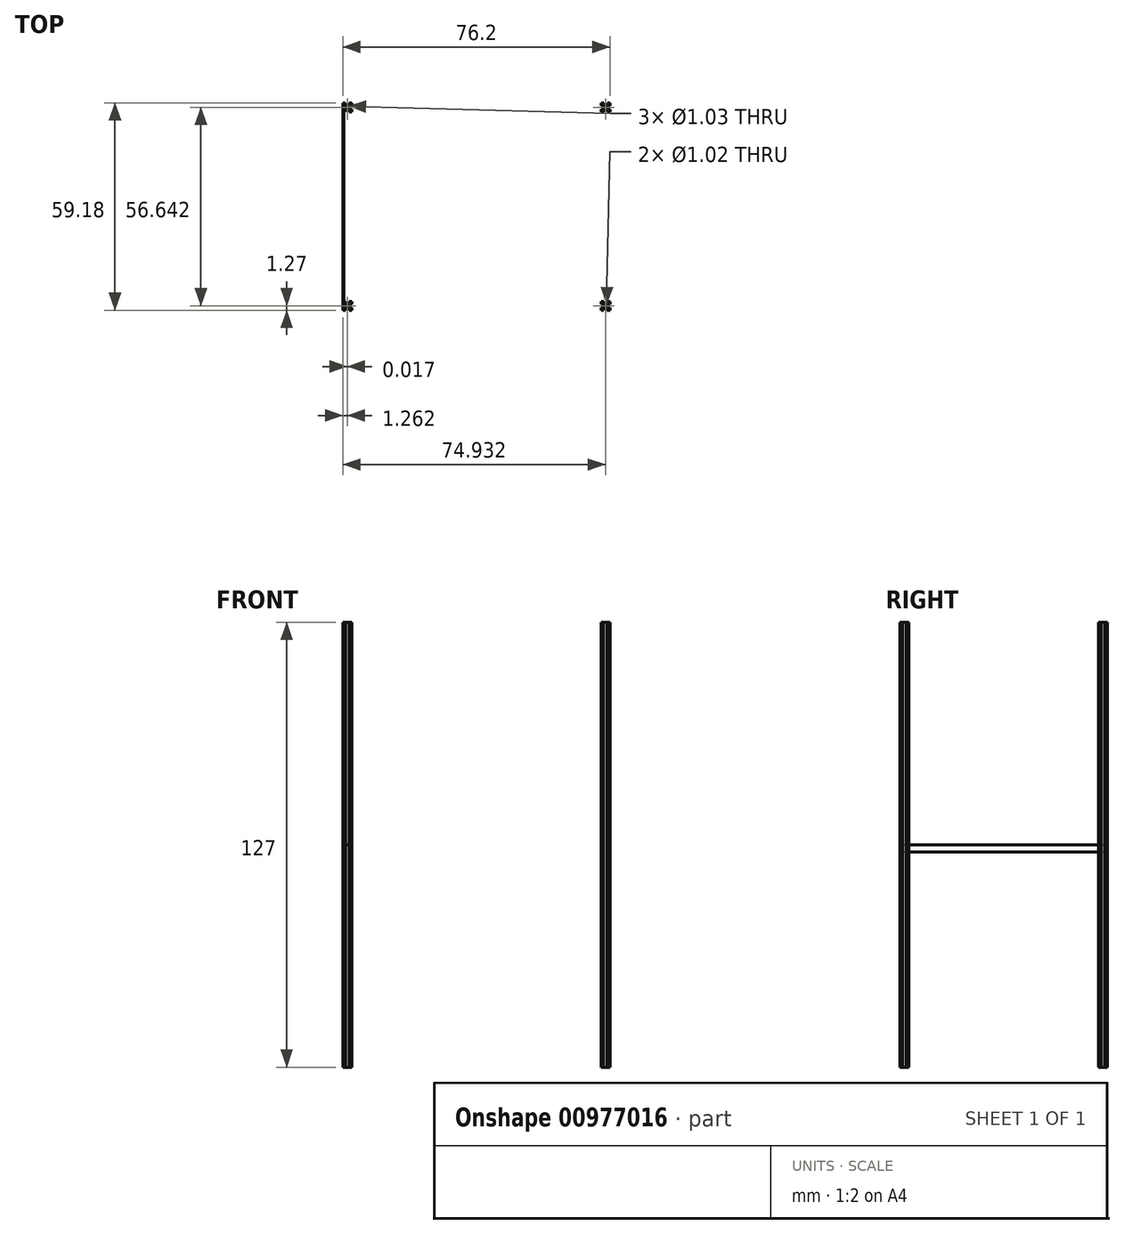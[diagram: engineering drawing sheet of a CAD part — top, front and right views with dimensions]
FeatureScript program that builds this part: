
annotation { "Feature Type Name" : "Feature", "Feature Type Description" : "" }
export const myFeature = defineFeature(function(context is Context, id is Id, definition is map)
    precondition{}
    {
        {
            var Q0;
            Q0=qCreatedBy(makeId("Top.planeOp"),FACE);
            var sketch = newSketch(context, id + "F0", { "sketchPlane" : qUnion([Q0])});
            skLineSegment(sketch, "E0.bottom", {"start": v(0, 0) * mm, "end": v(76.2, 0) * mm});
            skLineSegment(sketch, "E0.top", {"start": v(0, 59.18) * mm, "end": v(76.2, 59.18) * mm});
            skLineSegment(sketch, "E0.left", {"start": v(0, 0) * mm, "end": v(0, 59.18) * mm});
            skLineSegment(sketch, "E0.right", {"start": v(76.2, 0) * mm, "end": v(76.2, 59.18) * mm});
            skLineSegment(sketch, "E1.bottom", {"start": v(0, 59.18) * mm, "end": v(2.54, 59.18) * mm});
            skLineSegment(sketch, "E1.top", {"start": v(0, 56.64) * mm, "end": v(2.54, 56.64) * mm});
            skLineSegment(sketch, "E1.left", {"start": v(0, 59.18) * mm, "end": v(0, 56.64) * mm});
            skLineSegment(sketch, "E1.right", {"start": v(2.54, 59.18) * mm, "end": v(2.54, 56.64) * mm});
            skLineSegment(sketch, "E2.bottom", {"start": v(76.2, 59.18) * mm, "end": v(73.66, 59.18) * mm});
            skLineSegment(sketch, "E2.top", {"start": v(76.2, 56.64) * mm, "end": v(73.66, 56.64) * mm});
            skLineSegment(sketch, "E2.left", {"start": v(76.2, 59.18) * mm, "end": v(76.2, 56.64) * mm});
            skLineSegment(sketch, "E2.right", {"start": v(73.66, 59.18) * mm, "end": v(73.66, 56.64) * mm});
            skLineSegment(sketch, "E3.bottom", {"start": v(0, 0) * mm, "end": v(2.54, 0) * mm});
            skLineSegment(sketch, "E3.top", {"start": v(0, 2.54) * mm, "end": v(2.54, 2.54) * mm});
            skLineSegment(sketch, "E3.left", {"start": v(0, 0) * mm, "end": v(0, 2.54) * mm});
            skLineSegment(sketch, "E3.right", {"start": v(2.54, 0) * mm, "end": v(2.54, 2.54) * mm});
            skLineSegment(sketch, "E4.bottom", {"start": v(76.2, 0) * mm, "end": v(73.66, 0) * mm});
            skLineSegment(sketch, "E4.top", {"start": v(76.2, 2.54) * mm, "end": v(73.66, 2.54) * mm});
            skLineSegment(sketch, "E4.left", {"start": v(76.2, 0) * mm, "end": v(76.2, 2.54) * mm});
            skLineSegment(sketch, "E4.right", {"start": v(73.66, 0) * mm, "end": v(73.66, 2.54) * mm});
            skLineSegment(sketch, "E5", {"start": v(0, 57.91) * mm, "end": v(1.26, 57.91) * mm});
            skCircle(sketch, "E6", {"center": v(1.26, 57.91) * mm, "radius": 0.52 * mm});
            skLineSegment(sketch, "E7.bottom", {"start": v(0.74, 59.18) * mm, "end": v(1.79, 59.18) * mm});
            skLineSegment(sketch, "E7.top", {"start": v(0.74, 58.68) * mm, "end": v(1.79, 58.68) * mm});
            skLineSegment(sketch, "E7.left", {"start": v(0.74, 59.18) * mm, "end": v(0.74, 58.68) * mm});
            skLineSegment(sketch, "E7.right", {"start": v(1.79, 59.18) * mm, "end": v(1.79, 58.68) * mm});
            skLineSegment(sketch, "E8.bottom", {"start": v(2.54, 58.42) * mm, "end": v(2.04, 58.42) * mm});
            skLineSegment(sketch, "E8.top", {"start": v(2.54, 57.37) * mm, "end": v(2.04, 57.37) * mm});
            skLineSegment(sketch, "E8.left", {"start": v(2.54, 58.42) * mm, "end": v(2.54, 57.37) * mm});
            skLineSegment(sketch, "E8.right", {"start": v(2.04, 58.42) * mm, "end": v(2.04, 57.37) * mm});
            skLineSegment(sketch, "E9.bottom", {"start": v(0.74, 56.64) * mm, "end": v(1.79, 56.64) * mm});
            skLineSegment(sketch, "E9.top", {"start": v(0.74, 57.14) * mm, "end": v(1.79, 57.14) * mm});
            skLineSegment(sketch, "E9.left", {"start": v(0.74, 56.64) * mm, "end": v(0.74, 57.14) * mm});
            skLineSegment(sketch, "E9.right", {"start": v(1.79, 56.64) * mm, "end": v(1.79, 57.14) * mm});
            skLineSegment(sketch, "E10.bottom", {"start": v(0, 57.37) * mm, "end": v(0.5, 57.37) * mm});
            skLineSegment(sketch, "E10.top", {"start": v(0, 58.4) * mm, "end": v(0.5, 58.4) * mm});
            skLineSegment(sketch, "E10.left", {"start": v(0, 57.37) * mm, "end": v(0, 58.4) * mm});
            skLineSegment(sketch, "E10.right", {"start": v(0.5, 57.37) * mm, "end": v(0.5, 58.4) * mm});
            skLineSegment(sketch, "E11", {"start": v(73.66, 57.91) * mm, "end": v(74.93, 57.91) * mm});
            skCircle(sketch, "E12", {"center": v(74.93, 57.91) * mm, "radius": 0.5 * mm});
            skLineSegment(sketch, "E13.bottom", {"start": v(76.2, 58.39) * mm, "end": v(75.7, 58.39) * mm});
            skLineSegment(sketch, "E13.top", {"start": v(76.2, 57.38) * mm, "end": v(75.7, 57.38) * mm});
            skLineSegment(sketch, "E13.left", {"start": v(76.2, 58.39) * mm, "end": v(76.2, 57.38) * mm});
            skLineSegment(sketch, "E13.right", {"start": v(75.7, 58.39) * mm, "end": v(75.7, 57.38) * mm});
            skLineSegment(sketch, "E14.bottom", {"start": v(73.66, 57.38) * mm, "end": v(74.16, 57.38) * mm});
            skLineSegment(sketch, "E14.top", {"start": v(73.66, 58.4) * mm, "end": v(74.16, 58.4) * mm});
            skLineSegment(sketch, "E14.left", {"start": v(73.66, 57.38) * mm, "end": v(73.66, 58.4) * mm});
            skLineSegment(sketch, "E14.right", {"start": v(74.16, 57.38) * mm, "end": v(74.16, 58.4) * mm});
            skLineSegment(sketch, "E15", {"start": v(73.66, 1.27) * mm, "end": v(74.93, 1.27) * mm});
            skCircle(sketch, "E16", {"center": v(74.93, 1.27) * mm, "radius": 0.51 * mm});
            skLineSegment(sketch, "E17.bottom", {"start": v(76.2, 1.75) * mm, "end": v(75.7, 1.75) * mm});
            skLineSegment(sketch, "E17.top", {"start": v(76.2, 0.73) * mm, "end": v(75.7, 0.73) * mm});
            skLineSegment(sketch, "E17.left", {"start": v(76.2, 1.75) * mm, "end": v(76.2, 0.73) * mm});
            skLineSegment(sketch, "E17.right", {"start": v(75.7, 1.75) * mm, "end": v(75.7, 0.73) * mm});
            skLineSegment(sketch, "E18.bottom", {"start": v(73.66, 1.75) * mm, "end": v(74.16, 1.75) * mm});
            skLineSegment(sketch, "E18.top", {"start": v(73.66, 0.73) * mm, "end": v(74.16, 0.73) * mm});
            skLineSegment(sketch, "E18.left", {"start": v(73.66, 1.75) * mm, "end": v(73.66, 0.73) * mm});
            skLineSegment(sketch, "E18.right", {"start": v(74.16, 1.75) * mm, "end": v(74.16, 0.73) * mm});
            skLineSegment(sketch, "E19", {"start": v(0, 1.27) * mm, "end": v(1.28, 1.27) * mm});
            skCircle(sketch, "E20", {"center": v(1.28, 1.27) * mm, "radius": 0.51 * mm});
            skLineSegment(sketch, "E21.bottom", {"start": v(0.77, 2.54) * mm, "end": v(1.79, 2.54) * mm});
            skLineSegment(sketch, "E21.top", {"start": v(0.77, 2.04) * mm, "end": v(1.79, 2.04) * mm});
            skLineSegment(sketch, "E21.left", {"start": v(0.77, 2.54) * mm, "end": v(0.77, 2.04) * mm});
            skLineSegment(sketch, "E21.right", {"start": v(1.79, 2.54) * mm, "end": v(1.79, 2.04) * mm});
            skLineSegment(sketch, "E22.bottom", {"start": v(1.79, 0) * mm, "end": v(0.78, 0) * mm});
            skLineSegment(sketch, "E22.top", {"start": v(1.79, 0.5) * mm, "end": v(0.78, 0.5) * mm});
            skLineSegment(sketch, "E22.left", {"start": v(1.79, 0) * mm, "end": v(1.79, 0.5) * mm});
            skLineSegment(sketch, "E22.right", {"start": v(0.78, 0) * mm, "end": v(0.78, 0.5) * mm});
            skLineSegment(sketch, "E23.bottom", {"start": v(2.54, 1.75) * mm, "end": v(2.03, 1.75) * mm});
            skLineSegment(sketch, "E23.top", {"start": v(2.54, 0.74) * mm, "end": v(2.03, 0.74) * mm});
            skLineSegment(sketch, "E23.left", {"start": v(2.54, 1.75) * mm, "end": v(2.54, 0.74) * mm});
            skLineSegment(sketch, "E23.right", {"start": v(2.03, 1.75) * mm, "end": v(2.03, 0.74) * mm});
            skLineSegment(sketch, "E24.bottom", {"start": v(0, 0.74) * mm, "end": v(0.52, 0.74) * mm});
            skLineSegment(sketch, "E24.top", {"start": v(0, 1.75) * mm, "end": v(0.52, 1.75) * mm});
            skLineSegment(sketch, "E24.left", {"start": v(0, 0.74) * mm, "end": v(0, 1.75) * mm});
            skLineSegment(sketch, "E24.right", {"start": v(0.52, 0.74) * mm, "end": v(0.52, 1.75) * mm});
            skLineSegment(sketch, "E25", {"start": v(61.7, 59.18) * mm, "end": v(73.66, 59.18) * mm});
            skLineSegment(sketch, "E26", {"start": v(73.66, 58.4) * mm, "end": v(73.66, 59.18) * mm});
            skLineSegment(sketch, "E27", {"start": v(76.2, 57.38) * mm, "end": v(76.2, 56.64) * mm});
            skLineSegment(sketch, "E28", {"start": v(73.66, 59.18) * mm, "end": v(76.2, 59.18) * mm});
            skLineSegment(sketch, "E29.bottom", {"start": v(74.44, 59.18) * mm, "end": v(75.44, 59.18) * mm});
            skLineSegment(sketch, "E29.top", {"start": v(74.44, 58.67) * mm, "end": v(75.44, 58.67) * mm});
            skLineSegment(sketch, "E29.left", {"start": v(74.44, 59.18) * mm, "end": v(74.44, 58.67) * mm});
            skLineSegment(sketch, "E29.right", {"start": v(75.44, 59.18) * mm, "end": v(75.44, 58.67) * mm});
            skLineSegment(sketch, "E30.bottom", {"start": v(75.44, 56.64) * mm, "end": v(74.44, 56.64) * mm});
            skLineSegment(sketch, "E30.top", {"start": v(75.44, 57.16) * mm, "end": v(74.44, 57.16) * mm});
            skLineSegment(sketch, "E30.left", {"start": v(75.44, 56.64) * mm, "end": v(75.44, 57.16) * mm});
            skLineSegment(sketch, "E30.right", {"start": v(74.44, 56.64) * mm, "end": v(74.44, 57.16) * mm});
            skPoint(sketch, "E31.right.end.orphan", {"position": v(62.7, 58.68) * mm});
            skPoint(sketch, "E32.left.start.orphan", {"position": v(62.7, 56.64) * mm});
            skLineSegment(sketch, "E33.bottom", {"start": v(74.46, 2.54) * mm, "end": v(75.45, 2.54) * mm});
            skLineSegment(sketch, "E33.top", {"start": v(74.46, 2.04) * mm, "end": v(75.45, 2.04) * mm});
            skLineSegment(sketch, "E33.left", {"start": v(74.46, 2.54) * mm, "end": v(74.46, 2.04) * mm});
            skLineSegment(sketch, "E33.right", {"start": v(75.45, 2.54) * mm, "end": v(75.45, 2.04) * mm});
            skLineSegment(sketch, "E34.bottom", {"start": v(75.4, 0) * mm, "end": v(74.38, 0) * mm});
            skLineSegment(sketch, "E34.top", {"start": v(75.4, 0.52) * mm, "end": v(74.38, 0.52) * mm});
            skLineSegment(sketch, "E34.left", {"start": v(75.4, 0) * mm, "end": v(75.4, 0.52) * mm});
            skLineSegment(sketch, "E34.right", {"start": v(74.38, 0) * mm, "end": v(74.38, 0.52) * mm});
            skPoint(sketch, "E35.right.end.orphan", {"position": v(62.72, 2.04) * mm});
            skPoint(sketch, "E36.left.start.orphan", {"position": v(62.72, 0) * mm});
            skSolve(sketch);
        }
        {
            var Q0;
            Q0=makeQuery(id+"F0.imprint","IMPRINT",FACE,{"disambiguationData":[TD([[makeQuery(id+"F0.imprint","IMPRINT",EDGE,{"derivedFrom":sQuery(id+"F0.wireOp",EDGE,"E12")}),-1.0]])]});
            var Q1;
            Q1=makeQuery(id+"F0.imprint","IMPRINT",FACE,{"disambiguationData":[TD([[makeQuery(id+"F0.imprint","IMPRINT",EDGE,{"derivedFrom":sQuery(id+"F0.wireOp",EDGE,"E16")}),-1.0]])]});
            var Q2;
            Q2=makeQuery(id+"F0.imprint","IMPRINT",FACE,{"disambiguationData":[TD([[makeQuery(id+"F0.imprint","IMPRINT",EDGE,{"derivedFrom":sQuery(id+"F0.wireOp",EDGE,"E20")}),-1.0]])]});
            extrude(context, id + "F1", {"entities" : qUnion([Q0, Q1, Q2]), "depth" : 127 * mm, "offsetDistance" : 25.4 * mm});
        }
        {
            var Q0;
            Q0=qCreatedBy(makeId("Right.planeOp"),FACE);
            var sketch = newSketch(context, id + "F2", { "sketchPlane" : qUnion([Q0])});
            skLineSegment(sketch, "E37", {"start": v(0, 0) * mm, "end": v(0, 127) * mm});
            skLineSegment(sketch, "E38", {"start": v(0, 127) * mm, "end": v(0, 63.5) * mm});
            skLineSegment(sketch, "E39.bottom", {"start": v(0, 63.5) * mm, "end": v(59.18, 63.5) * mm});
            skLineSegment(sketch, "E39.top", {"start": v(0, 61.44) * mm, "end": v(59.18, 61.44) * mm});
            skLineSegment(sketch, "E39.left", {"start": v(0, 63.5) * mm, "end": v(0, 61.44) * mm});
            skLineSegment(sketch, "E39.right", {"start": v(59.18, 63.5) * mm, "end": v(59.18, 61.44) * mm});
            skSolve(sketch);
        }
        {
            var Q0;
            {var subQ0=sQuery(id+"F2.wireOp",EDGE,"E39.bottom");Q0=makeQuery(id+"F2.imprint","IMPRINT",FACE,{"disambiguationData":[TD([[makeQuery(id+"F2.imprint","IMPRINT",EDGE,{"derivedFrom":subQ0}),-1.0]])]});}
            extrude(context, id + "F3", {"entities" : qUnion([Q0]), "depth" : 0.25 * mm, "offsetDistance" : 25.4 * mm});
        }
        {
            var Q0;
            Q0=makeQuery(id+"F0.imprint","IMPRINT",FACE,{"disambiguationData":[TD([[makeQuery(id+"F0.imprint","IMPRINT",EDGE,{"derivedFrom":sQuery(id+"F0.wireOp",EDGE,"E20")}),-1.0]])]});
            var Q1;
            Q1=makeQuery(id+"F0.imprint","IMPRINT",FACE,{"disambiguationData":[TD([[makeQuery(id+"F0.imprint","IMPRINT",EDGE,{"derivedFrom":sQuery(id+"F0.wireOp",EDGE,"E6")}),-1.0]])]});
            extrude(context, id + "F4", {"entities" : qUnion([Q0, Q1]), "depth" : 63.5 * mm, "offsetDistance" : 25.4 * mm});
        }
    });
